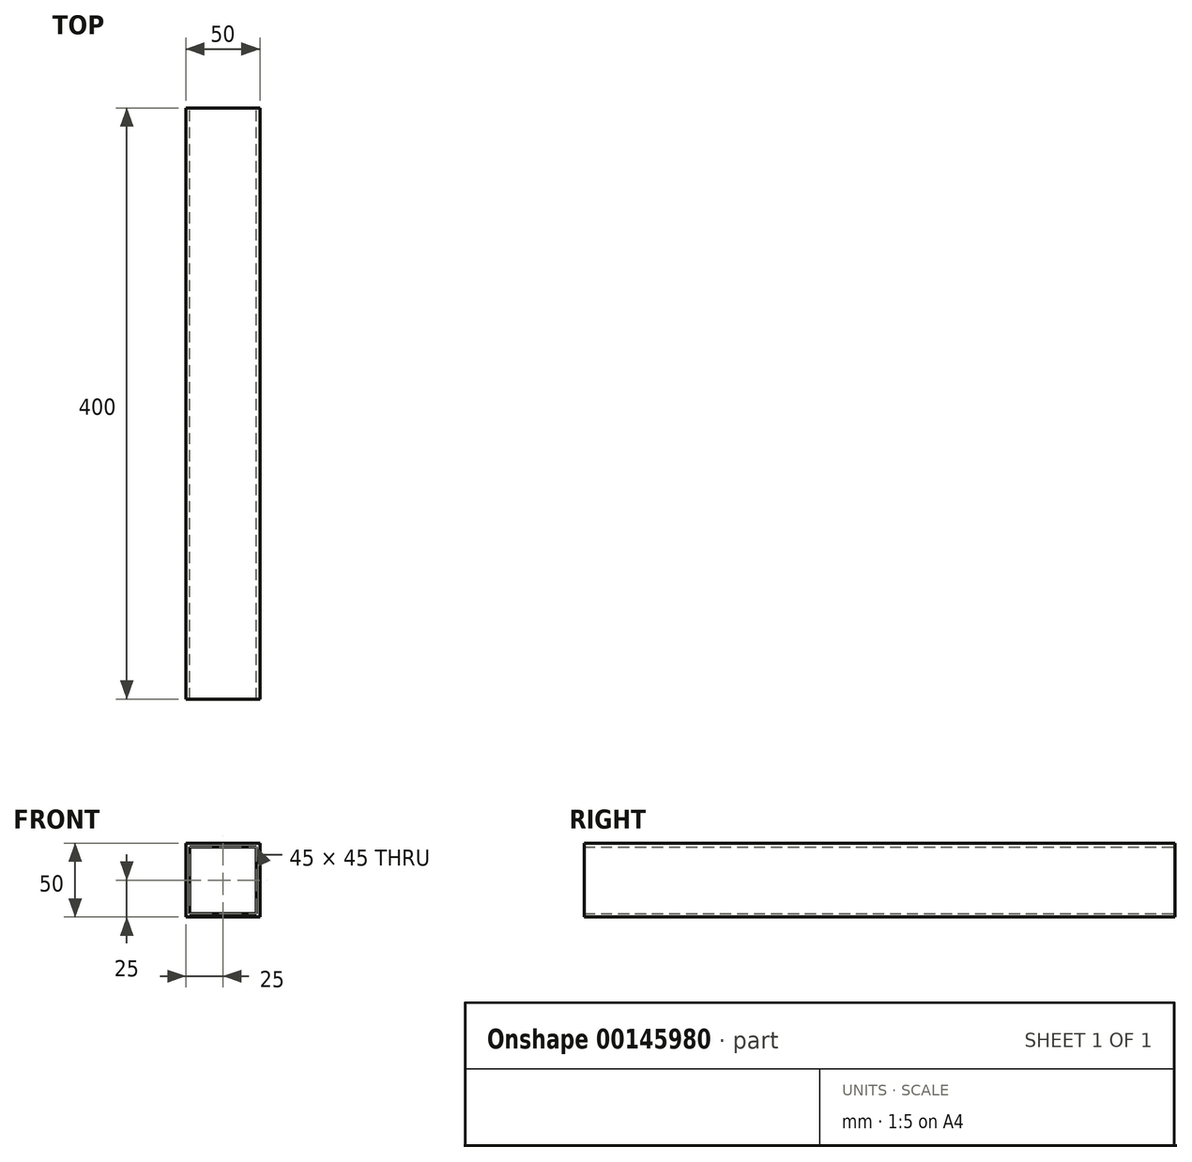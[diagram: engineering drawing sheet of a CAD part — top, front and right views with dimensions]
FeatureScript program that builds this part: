
annotation { "Feature Type Name" : "Feature", "Feature Type Description" : "" }
export const myFeature = defineFeature(function(context is Context, id is Id, definition is map)
    precondition{}
    {
        {
            var Q0;
            Q0=qCreatedBy(makeId("Front.planeOp"),FACE);
            var sketch = newSketch(context, id + "F0", { "sketchPlane" : qUnion([Q0])});
            skLineSegment(sketch, "E0.bottom", {"start": v(25, 25) * mm, "end": v(-25, 25) * mm});
            skLineSegment(sketch, "E0.top", {"start": v(25, -25) * mm, "end": v(-25, -25) * mm});
            skLineSegment(sketch, "E0.left", {"start": v(25, 25) * mm, "end": v(25, -25) * mm});
            skLineSegment(sketch, "E0.right", {"start": v(-25, 25) * mm, "end": v(-25, -25) * mm});
            skPoint(sketch, "E0.middle", {"position": v(0, 0) * mm});
            skLineSegment(sketch, "E1.bottom", {"start": v(22.5, 22.5) * mm, "end": v(-22.5, 22.5) * mm});
            skLineSegment(sketch, "E1.top", {"start": v(22.5, -22.5) * mm, "end": v(-22.5, -22.5) * mm});
            skLineSegment(sketch, "E1.left", {"start": v(22.5, 22.5) * mm, "end": v(22.5, -22.5) * mm});
            skLineSegment(sketch, "E1.right", {"start": v(-22.5, 22.5) * mm, "end": v(-22.5, -22.5) * mm});
            skSolve(sketch);
        }
        {
            var Q0;
            Q0=makeQuery(id+"F0.imprint","IMPRINT",FACE,{"disambiguationData":[TD([[makeQuery(id+"F0.imprint","IMPRINT",EDGE,{"derivedFrom":sQuery(id+"F0.wireOp",EDGE,"E0.bottom")}),1.0]])]});
            extrude(context, id + "F1", {"entities" : qUnion([Q0]), "depth" : 400 * mm});
        }
    });
